# Revit family: 879-100X1X-001-DN50-600
name_source: partatom
category: Pipe Accessories
units: mm (PartAtom-declared; Revit-internal decimal feet)

## family parameters
Always vertical = Yes
Cut with Voids When Loaded = No
Part Type = Valve - Breaks Into
Round Connector Dimension = Use Diameter
Shared = No
Work Plane-Based = No

## types (38) — shared parameters
1 = 1 mm  [stored 0.00328084 ft]
879-0050-10-14400051199 = DN50_PN10/16
879-0050-10-144000511A0 = DN50_PN10/16
879-0065-10-14400051199 = DN65_PN10/16
879-0065-10-144000511A0 = DN65_PN10/16
879-0080-10-14400051199 = DN80_PN10/16
879-0080-10-144000511A0 = DN80_PN10/16
879-0100-10-14400051199 = DN100_PN10/16
879-0100-10-144000511A0 = DN100_PN10/16
879-0150-10-14400051199 = DN150_PN10/16
879-0150-10-144000511A0 = DN150_PN10/16
879-0200-10-04400051199 = DN200_PN10
879-0200-10-044000511A0 = DN200_PN10
879-0200-10-14400051199 = DN200_PN16
879-0200-10-144000511A0 = DN200_PN16
879-0300-10-04400051199 = DN300_PN10
879-0300-10-044000511A0 = DN300_PN10
879-0300-10-14400051199 = DN300_PN16
879-0300-10-144000511A0 = DN300_PN16
879-0350-10-04400051199 = DN350_PN10
879-0350-10-044000511A0 = DN350_PN10
879-0350-10-14400051199 = DN350_PN16
879-0350-10-144000511A0 = DN350_PN16
879-0400-10-04400051199 = DN400_PN10
879-0400-10-044000511A0 = DN400_PN10
879-0400-10-14400051199 = DN400_PN16
879-0400-10-144000511A0 = DN400_PN16
879-0450-10-04400051199 = DN450_PN10
879-0450-10-044000511A0 = DN450_PN10
879-0450-10-14400051199 = DN450_PN16
879-0450-10-144000511A0 = DN450_PN16
879-0500-10-04400051199 = DN500_PN10
879-0500-10-044000511A0 = DN500_PN10
879-0500-10-14400051199 = DN500_PN16
879-0500-10-144000511A0 = DN500_PN16
879-0600-10-04400051199 = DN600_PN10
879-0600-10-044000511A0 = DN600_PN10
879-0600-10-14400051199 = DN600_PN16
879-0600-10-144000511A0 = DN600_PN16
Body_wall_thickness = 10 mm  [stored 0.0328084 ft]
Description_ = AVK PRESS. RED./PRESS. SUST. CONTROL VALVE
Search_Table = 879-100X1X-001-DN50-600
URL product pages = https://www.avkvalves.com

## per-type parameters (varying)
- 879-0050-10-14400051199_DN50_PN10/16: Body_Collar_Dia=24 mm; Body_Collar_Dia_2=21 mm  [stored 0.0688976 ft]; Body_Flange_Dia=66 mm; Body_Flange_Dia_2=72 mm; Body_Height_1=58 mm; Body_Height_2=29 mm; Body_Height_3=45 mm; Body_Height_4=44 mm; Body_Top_Dia=10 mm  [stored 0.0328084 ft]; Body_Top_Dia_2=9 mm  [stored 0.0295276 ft]; Body_With_Dia=46 mm; Body_With_Dia_1=58 mm; Body_With_Dia_2=62 mm; Bolt_support=177 mm; Bolt_support_2=88 mm; Bolt_support_Dia=12 mm  [stored 0.0393701 ft]; Bolt_support_lenght=45 mm; Bolt_support_lenght_2=55 mm; Bottom_profile=13 mm; D1=50 mm; D3=83 mm; D3_Ref=221 mm; DN=50 mm; Fillet_Length=6 mm  [stored 0.019685 ft]; Flange_thickness=19 mm  [stored 0.062336 ft]; H3=405 mm; ID=25 mm  [stored 0.082021 ft]; L=230 mm; PG_Dia=25 mm  [stored 0.082021 ft]; PG_Ref=38 mm; PG_depth=8 mm  [stored 0.0262467 ft]; PG_height=207 mm; PG_height_1=195 mm; PG_ref=45 mm; PR_1=41 mm  [stored 0.134514 ft]; P_lenght=25 mm  [stored 0.082021 ft]; Pilot_Dia_1=15 mm  [stored 0.0492126 ft]; Pilot_Dia_2=23 mm  [stored 0.0754593 ft]; Pilot_Dia_3=10 mm  [stored 0.0328084 ft]; Pilot_Dia_4=5 mm  [stored 0.0164042 ft]; Pilot_Dia_5=3 mm  [stored 0.00984252 ft]; Pilot_top_1=234 mm; Pilot_top_ref=78 mm; Profile1_Height=100 mm; Profile1_Length=22 mm  [stored 0.0721785 ft]; Profile1_Length_2=15 mm  [stored 0.0492126 ft]; Profile_Dia=6 mm  [stored 0.019685 ft]; Profile_Dia_2=6 mm  [stored 0.019685 ft]; Profile_Dia_3=12 mm  [stored 0.0393701 ft]; Profile_height ref=41 mm  [stored 0.134514 ft]; T_Height=182 mm; T_Height_2=156 mm; T_Height_Ref_1=26 mm; T_Height_Ref_2=30 mm  [stored 0.0984252 ft]; Top_Profile=106 mm; Top_Profile_Ref=111 mm; W=295 mm; W_Ref=199 mm; W_ref_2=277 mm
- 879-0050-10-144000511A0_DN50_PN10/16: Body_Collar_Dia=24 mm; Body_Collar_Dia_2=21 mm  [stored 0.0688976 ft]; Body_Flange_Dia=66 mm; Body_Flange_Dia_2=72 mm; Body_Height_1=58 mm; Body_Height_2=29 mm; Body_Height_3=50 mm; Body_Height_4=44 mm; Body_Top_Dia=10 mm  [stored 0.0328084 ft]; Body_Top_Dia_2=9 mm  [stored 0.0295276 ft]; Body_With_Dia=46 mm; Body_With_Dia_1=58 mm; Body_With_Dia_2=62 mm; Bolt_support=177 mm; Bolt_support_2=88 mm; Bolt_support_Dia=12 mm  [stored 0.0393701 ft]; Bolt_support_lenght=45 mm; Bolt_support_lenght_2=55 mm; Bottom_profile=13 mm; D1=50 mm; D3=83 mm; D3_Ref=221 mm; DN=50 mm; Fillet_Length=6 mm  [stored 0.019685 ft]; Flange_thickness=19 mm  [stored 0.062336 ft]; H3=407 mm; ID=25 mm  [stored 0.082021 ft]; L=230 mm; PG_Dia=25 mm  [stored 0.082021 ft]; PG_Ref=38 mm; PG_depth=8 mm  [stored 0.0262467 ft]; PG_height=215 mm; PG_height_1=203 mm; PG_ref=45 mm; PR_1=39 mm; P_lenght=25 mm  [stored 0.082021 ft]; Pilot_Dia_1=15 mm  [stored 0.0492126 ft]; Pilot_Dia_2=23 mm  [stored 0.0754593 ft]; Pilot_Dia_3=10 mm  [stored 0.0328084 ft]; Pilot_Dia_4=5 mm  [stored 0.0164042 ft]; Pilot_Dia_5=3 mm  [stored 0.00984252 ft]; Pilot_top_1=238 mm; Pilot_top_ref=77 mm; Profile1_Height=110 mm; Profile1_Length=22 mm  [stored 0.0721785 ft]; Profile1_Length_2=15 mm  [stored 0.0492126 ft]; Profile_Dia=6 mm  [stored 0.019685 ft]; Profile_Dia_2=6 mm  [stored 0.019685 ft]; Profile_Dia_3=12 mm  [stored 0.0393701 ft]; Profile_height ref=41 mm  [stored 0.134514 ft]; T_Height=174 mm; T_Height_2=149 mm; T_Height_Ref_1=25 mm  [stored 0.082021 ft]; T_Height_Ref_2=29 mm; Top_Profile=106 mm; Top_Profile_Ref=111 mm; W=295 mm; W_Ref=199 mm; W_ref_2=277 mm
- 879-0065-10-14400051199_DN65_PN10/16: Body_Collar_Dia=30 mm  [stored 0.0984252 ft]; Body_Collar_Dia_2=26 mm; Body_Flange_Dia=83 mm; Body_Flange_Dia_2=91 mm; Body_Height_1=73 mm; Body_Height_2=36 mm  [stored 0.11811 ft]; Body_Height_3=58 mm; Body_Height_4=51 mm; Body_Top_Dia=13 mm; Body_Top_Dia_2=11 mm; Body_With_Dia=58 mm; Body_With_Dia_1=73 mm; Body_With_Dia_2=78 mm; Bolt_support=223 mm; Bolt_support_2=112 mm; Bolt_support_Dia=12 mm  [stored 0.0393701 ft]; Bolt_support_lenght=53 mm; Bolt_support_lenght_2=63 mm; Bottom_profile=16 mm  [stored 0.0524934 ft]; D1=59 mm; D3=93 mm; D3_Ref=246 mm; DN=65 mm; Fillet_Length=6 mm  [stored 0.019685 ft]; Flange_thickness=19 mm  [stored 0.062336 ft]; H3=435 mm; ID=33 mm  [stored 0.108268 ft]; L=290 mm; PG_Dia=33 mm  [stored 0.108268 ft]; PG_Ref=48 mm; PG_depth=8 mm  [stored 0.0262467 ft]; PG_height=232 mm; PG_height_1=216 mm; PG_ref=53 mm; PR_1=42 mm  [stored 0.137795 ft]; P_lenght=29 mm; Pilot_Dia_1=18 mm; Pilot_Dia_2=26 mm; Pilot_Dia_3=12 mm  [stored 0.0393701 ft]; Pilot_Dia_4=6 mm  [stored 0.019685 ft]; Pilot_Dia_5=4 mm  [stored 0.0131234 ft]; Pilot_top_1=262 mm; Pilot_top_ref=70 mm; Profile1_Height=117 mm; Profile1_Length=25 mm  [stored 0.082021 ft]; Profile1_Length_2=17 mm; Profile_Dia=6 mm  [stored 0.019685 ft]; Profile_Dia_2=6 mm  [stored 0.019685 ft]; Profile_Dia_3=12 mm  [stored 0.0393701 ft]; Profile_height ref=41 mm  [stored 0.134514 ft]; T_Height=185 mm; T_Height_2=158 mm; T_Height_Ref_1=26 mm; T_Height_Ref_2=31 mm  [stored 0.101706 ft]; Top_Profile=134 mm; Top_Profile_Ref=139 mm; W=325 mm; W_Ref=220 mm; W_ref_2=307 mm
- 879-0065-10-144000511A0_DN65_PN10/16: Body_Collar_Dia=30 mm  [stored 0.0984252 ft]; Body_Collar_Dia_2=26 mm; Body_Flange_Dia=83 mm; Body_Flange_Dia_2=91 mm; Body_Height_1=73 mm; Body_Height_2=36 mm  [stored 0.11811 ft]; Body_Height_3=73 mm; Body_Height_4=51 mm; Body_Top_Dia=13 mm; Body_Top_Dia_2=11 mm; Body_With_Dia=58 mm; Body_With_Dia_1=73 mm; Body_With_Dia_2=78 mm; Bolt_support=223 mm; Bolt_support_2=112 mm; Bolt_support_Dia=12 mm  [stored 0.0393701 ft]; Bolt_support_lenght=53 mm; Bolt_support_lenght_2=63 mm; Bottom_profile=16 mm  [stored 0.0524934 ft]; D1=59 mm; D3=93 mm; D3_Ref=246 mm; DN=65 mm; Fillet_Length=6 mm  [stored 0.019685 ft]; Flange_thickness=19 mm  [stored 0.062336 ft]; H3=436 mm; ID=33 mm  [stored 0.108268 ft]; L=290 mm; PG_Dia=33 mm  [stored 0.108268 ft]; PG_Ref=48 mm; PG_depth=8 mm  [stored 0.0262467 ft]; PG_height=246 mm; PG_height_1=230 mm; PG_ref=53 mm; PR_1=38 mm; P_lenght=29 mm; Pilot_Dia_1=18 mm; Pilot_Dia_2=26 mm; Pilot_Dia_3=12 mm  [stored 0.0393701 ft]; Pilot_Dia_4=6 mm  [stored 0.019685 ft]; Pilot_Dia_5=4 mm  [stored 0.0131234 ft]; Pilot_top_1=270 mm; Pilot_top_ref=64 mm; Profile1_Height=135 mm; Profile1_Length=25 mm  [stored 0.082021 ft]; Profile1_Length_2=17 mm; Profile_Dia=6 mm  [stored 0.019685 ft]; Profile_Dia_2=6 mm  [stored 0.019685 ft]; Profile_Dia_3=12 mm  [stored 0.0393701 ft]; Profile_height ref=41 mm  [stored 0.134514 ft]; T_Height=168 mm; T_Height_2=144 mm; T_Height_Ref_1=24 mm; T_Height_Ref_2=28 mm  [stored 0.0918635 ft]; Top_Profile=134 mm; Top_Profile_Ref=139 mm; W=325 mm; W_Ref=220 mm; W_ref_2=307 mm
- 879-0080-10-14400051199_DN80_PN10/16: Body_Collar_Dia=32 mm; Body_Collar_Dia_2=28 mm  [stored 0.0918635 ft]; Body_Flange_Dia=89 mm; Body_Flange_Dia_2=97 mm; Body_Height_1=78 mm; Body_Height_2=39 mm; Body_Height_3=62 mm; Body_Height_4=54 mm; Body_Top_Dia=14 mm  [stored 0.0459318 ft]; Body_Top_Dia_2=12 mm  [stored 0.0393701 ft]; Body_With_Dia=62 mm; Body_With_Dia_1=78 mm; Body_With_Dia_2=84 mm; Bolt_support=238 mm; Bolt_support_2=119 mm; Bolt_support_Dia=12 mm  [stored 0.0393701 ft]; Bolt_support_lenght=60 mm; Bolt_support_lenght_2=70 mm; Bottom_profile=20 mm  [stored 0.0656168 ft]; D1=66 mm; D3=100 mm; D3_Ref=264 mm; DN=80 mm; Fillet_Length=6 mm  [stored 0.019685 ft]; Flange_thickness=19 mm  [stored 0.062336 ft]; H3=450 mm; ID=40 mm  [stored 0.131234 ft]; L=310 mm; PG_Dia=40 mm  [stored 0.131234 ft]; PG_Ref=52 mm; PG_depth=8 mm  [stored 0.0262467 ft]; PG_height=262 mm; PG_height_1=242 mm; PG_ref=60 mm; PR_1=37 mm; P_lenght=32 mm; Pilot_Dia_1=20 mm  [stored 0.0656168 ft]; Pilot_Dia_2=29 mm; Pilot_Dia_3=13 mm; Pilot_Dia_4=7 mm  [stored 0.0229659 ft]; Pilot_Dia_5=4 mm  [stored 0.0131234 ft]; Pilot_top_1=272 mm; Pilot_top_ref=68 mm; Profile1_Height=144 mm; Profile1_Length=27 mm; Profile1_Length_2=18 mm; Profile_Dia=6 mm  [stored 0.019685 ft]; Profile_Dia_2=6 mm  [stored 0.019685 ft]; Profile_Dia_3=12 mm  [stored 0.0393701 ft]; Profile_height ref=41 mm  [stored 0.134514 ft]; T_Height=165 mm; T_Height_2=141 mm; T_Height_Ref_1=24 mm; T_Height_Ref_2=28 mm  [stored 0.0918635 ft]; Top_Profile=143 mm; Top_Profile_Ref=148 mm; W=345 mm; W_Ref=234 mm; W_ref_2=327 mm
- 879-0080-10-144000511A0_DN80_PN10/16: Body_Collar_Dia=32 mm; Body_Collar_Dia_2=28 mm  [stored 0.0918635 ft]; Body_Flange_Dia=89 mm; Body_Flange_Dia_2=97 mm; Body_Height_1=78 mm; Body_Height_2=39 mm; Body_Height_3=78 mm; Body_Height_4=54 mm; Body_Top_Dia=14 mm  [stored 0.0459318 ft]; Body_Top_Dia_2=12 mm  [stored 0.0393701 ft]; Body_With_Dia=62 mm; Body_With_Dia_1=78 mm; Body_With_Dia_2=84 mm; Bolt_support=238 mm; Bolt_support_2=119 mm; Bolt_support_Dia=12 mm  [stored 0.0393701 ft]; Bolt_support_lenght=60 mm; Bolt_support_lenght_2=70 mm; Bottom_profile=20 mm  [stored 0.0656168 ft]; D1=66 mm; D3=100 mm; D3_Ref=264 mm; DN=80 mm; Fillet_Length=6 mm  [stored 0.019685 ft]; Flange_thickness=19 mm  [stored 0.062336 ft]; H3=451 mm; ID=40 mm  [stored 0.131234 ft]; L=310 mm; PG_Dia=40 mm  [stored 0.131234 ft]; PG_Ref=52 mm; PG_depth=8 mm  [stored 0.0262467 ft]; PG_height=254 mm; PG_height_1=234 mm; PG_ref=60 mm; PR_1=40 mm  [stored 0.131234 ft]; P_lenght=32 mm; Pilot_Dia_1=20 mm  [stored 0.0656168 ft]; Pilot_Dia_2=29 mm; Pilot_Dia_3=13 mm; Pilot_Dia_4=7 mm  [stored 0.0229659 ft]; Pilot_Dia_5=4 mm  [stored 0.0131234 ft]; Pilot_top_1=280 mm; Pilot_top_ref=61 mm; Profile1_Height=133 mm; Profile1_Length=27 mm; Profile1_Length_2=18 mm; Profile_Dia=6 mm  [stored 0.019685 ft]; Profile_Dia_2=6 mm  [stored 0.019685 ft]; Profile_Dia_3=12 mm  [stored 0.0393701 ft]; Profile_height ref=41 mm  [stored 0.134514 ft]; T_Height=177 mm; T_Height_2=152 mm; T_Height_Ref_1=25 mm  [stored 0.082021 ft]; T_Height_Ref_2=30 mm  [stored 0.0984252 ft]; Top_Profile=143 mm; Top_Profile_Ref=148 mm; W=345 mm; W_Ref=234 mm; W_ref_2=327 mm
- 879-0100-10-14400051199_DN100_PN10/16: Body_Collar_Dia=36 mm  [stored 0.11811 ft]; Body_Collar_Dia_2=31 mm  [stored 0.101706 ft]; Body_Flange_Dia=100 mm; Body_Flange_Dia_2=109 mm; Body_Height_1=88 mm; Body_Height_2=44 mm; Body_Height_3=59 mm; Body_Height_4=59 mm; Body_Top_Dia=16 mm  [stored 0.0524934 ft]; Body_Top_Dia_2=13 mm; Body_With_Dia=70 mm; Body_With_Dia_1=88 mm; Body_With_Dia_2=95 mm; Bolt_support=269 mm; Bolt_support_2=135 mm; Bolt_support_Dia=12 mm  [stored 0.0393701 ft]; Bolt_support_lenght=70 mm; Bolt_support_lenght_2=80 mm; Bottom_profile=25 mm  [stored 0.082021 ft]; D1=78 mm; D3=110 mm; D3_Ref=296 mm; DN=100 mm; Fillet_Length=6 mm  [stored 0.019685 ft]; Flange_thickness=19 mm  [stored 0.062336 ft]; H3=470 mm; ID=50 mm; L=350 mm; PG_Dia=50 mm; PG_Ref=58 mm; PG_depth=8 mm  [stored 0.0262467 ft]; PG_height=279 mm; PG_height_1=254 mm; PG_ref=70 mm; PR_1=38 mm; P_lenght=36 mm  [stored 0.11811 ft]; Pilot_Dia_1=22 mm  [stored 0.0721785 ft]; Pilot_Dia_2=33 mm  [stored 0.108268 ft]; Pilot_Dia_3=15 mm  [stored 0.0492126 ft]; Pilot_Dia_4=7 mm  [stored 0.0229659 ft]; Pilot_Dia_5=5 mm  [stored 0.0164042 ft]; Pilot_top_1=282 mm; Pilot_top_ref=68 mm; Profile1_Height=150 mm; Profile1_Length=30 mm  [stored 0.0984252 ft]; Profile1_Length_2=20 mm  [stored 0.0656168 ft]; Profile_Dia=6 mm  [stored 0.019685 ft]; Profile_Dia_2=6 mm  [stored 0.019685 ft]; Profile_Dia_3=12 mm  [stored 0.0393701 ft]; Profile_height ref=41 mm  [stored 0.134514 ft]; T_Height=169 mm; T_Height_2=145 mm; T_Height_Ref_1=24 mm; T_Height_Ref_2=28 mm  [stored 0.0918635 ft]; Top_Profile=162 mm; Top_Profile_Ref=167 mm; W=390 mm; W_Ref=263 mm; W_ref_2=372 mm
- 879-0100-10-144000511A0_DN100_PN10/16: Body_Collar_Dia=36 mm  [stored 0.11811 ft]; Body_Collar_Dia_2=31 mm  [stored 0.101706 ft]; Body_Flange_Dia=100 mm; Body_Flange_Dia_2=109 mm; Body_Height_1=88 mm; Body_Height_2=44 mm; Body_Height_3=70 mm; Body_Height_4=59 mm; Body_Top_Dia=16 mm  [stored 0.0524934 ft]; Body_Top_Dia_2=13 mm; Body_With_Dia=70 mm; Body_With_Dia_1=88 mm; Body_With_Dia_2=95 mm; Bolt_support=269 mm; Bolt_support_2=135 mm; Bolt_support_Dia=12 mm  [stored 0.0393701 ft]; Bolt_support_lenght=70 mm; Bolt_support_lenght_2=80 mm; Bottom_profile=25 mm  [stored 0.082021 ft]; D1=78 mm; D3=110 mm; D3_Ref=296 mm; DN=100 mm; Fillet_Length=6 mm  [stored 0.019685 ft]; Flange_thickness=19 mm  [stored 0.062336 ft]; H3=474 mm; ID=50 mm; L=350 mm; PG_Dia=50 mm; PG_Ref=58 mm; PG_depth=8 mm  [stored 0.0262467 ft]; PG_height=273 mm; PG_height_1=248 mm; PG_ref=70 mm; PR_1=41 mm  [stored 0.134514 ft]; P_lenght=36 mm  [stored 0.11811 ft]; Pilot_Dia_1=22 mm  [stored 0.0721785 ft]; Pilot_Dia_2=33 mm  [stored 0.108268 ft]; Pilot_Dia_3=15 mm  [stored 0.0492126 ft]; Pilot_Dia_4=7 mm  [stored 0.0229659 ft]; Pilot_Dia_5=5 mm  [stored 0.0164042 ft]; Pilot_top_1=290 mm; Pilot_top_ref=64 mm; Profile1_Height=141 mm; Profile1_Length=30 mm  [stored 0.0984252 ft]; Profile1_Length_2=20 mm  [stored 0.0656168 ft]; Profile_Dia=6 mm  [stored 0.019685 ft]; Profile_Dia_2=6 mm  [stored 0.019685 ft]; Profile_Dia_3=12 mm  [stored 0.0393701 ft]; Profile_height ref=41 mm  [stored 0.134514 ft]; T_Height=182 mm; T_Height_2=156 mm; T_Height_Ref_1=26 mm; T_Height_Ref_2=30 mm  [stored 0.0984252 ft]; Top_Profile=162 mm; Top_Profile_Ref=167 mm; W=390 mm; W_Ref=263 mm; W_ref_2=372 mm
- 879-0150-10-14400051199_DN150_PN10/16: Body_Collar_Dia=50 mm; Body_Collar_Dia_2=43 mm; Body_Flange_Dia=137 mm; Body_Flange_Dia_2=150 mm; Body_Height_1=120 mm; Body_Height_2=60 mm; Body_Height_3=60 mm; Body_Height_4=75 mm; Body_Top_Dia=22 mm  [stored 0.0721785 ft]; Body_Top_Dia_2=18 mm; Body_With_Dia=96 mm; Body_With_Dia_1=120 mm; Body_With_Dia_2=130 mm; Bolt_support=369 mm; Bolt_support_2=185 mm; Bolt_support_Dia=16 mm  [stored 0.0524934 ft]; Bolt_support_lenght=95 mm; Bolt_support_lenght_2=105 mm; Bottom_profile=38 mm; D1=106 mm; D3=143 mm; D3_Ref=373 mm; DN=150 mm; Fillet_Length=8 mm  [stored 0.0262467 ft]; Flange_thickness=19 mm  [stored 0.062336 ft]; H3=605 mm; ID=75 mm; L=480 mm; PG_Dia=50 mm; PG_Ref=80 mm; PG_depth=11 mm; PG_height=339 mm; PG_height_1=314 mm; PG_ref=95 mm; PR_1=51 mm; P_lenght=51 mm; Pilot_Dia_1=31 mm  [stored 0.101706 ft]; Pilot_Dia_2=47 mm; Pilot_Dia_3=21 mm  [stored 0.0688976 ft]; Pilot_Dia_4=10 mm  [stored 0.0328084 ft]; Pilot_Dia_5=7 mm  [stored 0.0229659 ft]; Pilot_top_1=359 mm; Pilot_top_ref=94 mm; Profile1_Height=195 mm; Profile1_Length=39 mm; Profile1_Length_2=26 mm; Profile_Dia=8 mm  [stored 0.0262467 ft]; Profile_Dia_2=8 mm  [stored 0.0262467 ft]; Profile_Dia_3=16 mm  [stored 0.0524934 ft]; Profile_height ref=43 mm; T_Height=225 mm; T_Height_2=192 mm; T_Height_Ref_1=32 mm; T_Height_Ref_2=37 mm; Top_Profile=222 mm; Top_Profile_Ref=227 mm; W=485 mm; W_Ref=327 mm; W_ref_2=461 mm
- 879-0150-10-144000511A0_DN150_PN10/16: Body_Collar_Dia=50 mm; Body_Collar_Dia_2=43 mm; Body_Flange_Dia=137 mm; Body_Flange_Dia_2=150 mm; Body_Height_1=120 mm; Body_Height_2=60 mm; Body_Height_3=68 mm; Body_Height_4=75 mm; Body_Top_Dia=22 mm  [stored 0.0721785 ft]; Body_Top_Dia_2=18 mm; Body_With_Dia=96 mm; Body_With_Dia_1=120 mm; Body_With_Dia_2=130 mm; Bolt_support=369 mm; Bolt_support_2=185 mm; Bolt_support_Dia=16 mm  [stored 0.0524934 ft]; Bolt_support_lenght=95 mm; Bolt_support_lenght_2=105 mm; Bottom_profile=38 mm; D1=106 mm; D3=143 mm; D3_Ref=373 mm; DN=150 mm; Fillet_Length=8 mm  [stored 0.0262467 ft]; Flange_thickness=19 mm  [stored 0.062336 ft]; H3=607 mm; ID=75 mm; L=480 mm; PG_Dia=50 mm; PG_Ref=80 mm; PG_depth=11 mm; PG_height=339 mm; PG_height_1=314 mm; PG_ref=95 mm; PR_1=51 mm; P_lenght=51 mm; Pilot_Dia_1=31 mm  [stored 0.101706 ft]; Pilot_Dia_2=47 mm; Pilot_Dia_3=21 mm  [stored 0.0688976 ft]; Pilot_Dia_4=10 mm  [stored 0.0328084 ft]; Pilot_Dia_5=7 mm  [stored 0.0229659 ft]; Pilot_top_1=364 mm; Pilot_top_ref=91 mm; Profile1_Height=195 mm; Profile1_Length=39 mm; Profile1_Length_2=26 mm; Profile_Dia=8 mm  [stored 0.0262467 ft]; Profile_Dia_2=8 mm  [stored 0.0262467 ft]; Profile_Dia_3=16 mm  [stored 0.0524934 ft]; Profile_height ref=43 mm; T_Height=227 mm; T_Height_2=194 mm; T_Height_Ref_1=32 mm; T_Height_Ref_2=38 mm; Top_Profile=222 mm; Top_Profile_Ref=227 mm; W=485 mm; W_Ref=327 mm; W_ref_2=461 mm
- 879-0200-10-04400051199_DN200_PN10: Body_Collar_Dia=63 mm; Body_Collar_Dia_2=54 mm; Body_Flange_Dia=171 mm; Body_Flange_Dia_2=188 mm; Body_Height_1=150 mm; Body_Height_2=75 mm; Body_Height_3=75 mm; Body_Height_4=90 mm; Body_Top_Dia=27 mm; Body_Top_Dia_2=22 mm  [stored 0.0721785 ft]; Body_With_Dia=120 mm; Body_With_Dia_1=150 mm; Body_With_Dia_2=162 mm; Bolt_support=462 mm; Bolt_support_2=231 mm; Bolt_support_Dia=20 mm  [stored 0.0656168 ft]; Bolt_support_lenght=120 mm; Bolt_support_lenght_2=130 mm; Bottom_profile=50 mm; D1=133 mm; D3=170 mm; D3_Ref=428 mm; DN=200 mm; Fillet_Length=10 mm  [stored 0.0328084 ft]; Flange_thickness=20 mm  [stored 0.0656168 ft]; H3=720 mm; ID=100 mm; L=600 mm; PG_Dia=67 mm; PG_Ref=100 mm; PG_depth=14 mm  [stored 0.0459318 ft]; PG_height=410 mm; PG_height_1=377 mm; PG_ref=120 mm; PR_1=60 mm; P_lenght=64 mm; Pilot_Dia_1=39 mm; Pilot_Dia_2=58 mm; Pilot_Dia_3=26 mm; Pilot_Dia_4=13 mm; Pilot_Dia_5=9 mm  [stored 0.0295276 ft]; Pilot_top_1=433 mm; Pilot_top_ref=108 mm; Profile1_Height=238 mm; Profile1_Length=46 mm; Profile1_Length_2=31 mm  [stored 0.101706 ft]; Profile_Dia=10 mm  [stored 0.0328084 ft]; Profile_Dia_2=10 mm  [stored 0.0328084 ft]; Profile_Dia_3=20 mm  [stored 0.0656168 ft]; Profile_height ref=45 mm; T_Height=267 mm; T_Height_2=229 mm; T_Height_Ref_1=38 mm; T_Height_Ref_2=45 mm; Top_Profile=277 mm; Top_Profile_Ref=282 mm; W=545 mm; W_Ref=370 mm; W_ref_2=515 mm
- 879-0200-10-044000511A0_DN200_PN10: Body_Collar_Dia=63 mm; Body_Collar_Dia_2=54 mm; Body_Flange_Dia=171 mm; Body_Flange_Dia_2=188 mm; Body_Height_1=150 mm; Body_Height_2=75 mm; Body_Height_3=100 mm; Body_Height_4=90 mm; Body_Top_Dia=27 mm; Body_Top_Dia_2=22 mm  [stored 0.0721785 ft]; Body_With_Dia=120 mm; Body_With_Dia_1=150 mm; Body_With_Dia_2=162 mm; Bolt_support=462 mm; Bolt_support_2=231 mm; Bolt_support_Dia=20 mm  [stored 0.0656168 ft]; Bolt_support_lenght=120 mm; Bolt_support_lenght_2=130 mm; Bottom_profile=50 mm; D1=133 mm; D3=170 mm; D3_Ref=428 mm; DN=200 mm; Fillet_Length=10 mm  [stored 0.0328084 ft]; Flange_thickness=20 mm  [stored 0.0656168 ft]; H3=774 mm; ID=100 mm; L=600 mm; PG_Dia=67 mm; PG_Ref=100 mm; PG_depth=14 mm  [stored 0.0459318 ft]; PG_height=424 mm; PG_height_1=391 mm; PG_ref=120 mm; PR_1=72 mm; P_lenght=64 mm; Pilot_Dia_1=39 mm; Pilot_Dia_2=58 mm; Pilot_Dia_3=26 mm; Pilot_Dia_4=13 mm; Pilot_Dia_5=9 mm  [stored 0.0295276 ft]; Pilot_top_1=472 mm; Pilot_top_ref=122 mm; Profile1_Height=240 mm; Profile1_Length=46 mm; Profile1_Length_2=31 mm  [stored 0.101706 ft]; Profile_Dia=10 mm  [stored 0.0328084 ft]; Profile_Dia_2=10 mm  [stored 0.0328084 ft]; Profile_Dia_3=20 mm  [stored 0.0656168 ft]; Profile_height ref=45 mm; T_Height=319 mm; T_Height_2=273 mm; T_Height_Ref_1=46 mm; T_Height_Ref_2=53 mm; Top_Profile=277 mm; Top_Profile_Ref=282 mm; W=545 mm; W_Ref=370 mm; W_ref_2=515 mm
- 879-0200-10-14400051199_DN200_PN16: Body_Collar_Dia=63 mm; Body_Collar_Dia_2=54 mm; Body_Flange_Dia=171 mm; Body_Flange_Dia_2=188 mm; Body_Height_1=150 mm; Body_Height_2=75 mm; Body_Height_3=75 mm; Body_Height_4=90 mm; Body_Top_Dia=27 mm; Body_Top_Dia_2=22 mm  [stored 0.0721785 ft]; Body_With_Dia=120 mm; Body_With_Dia_1=150 mm; Body_With_Dia_2=162 mm; Bolt_support=462 mm; Bolt_support_2=231 mm; Bolt_support_Dia=20 mm  [stored 0.0656168 ft]; Bolt_support_lenght=120 mm; Bolt_support_lenght_2=130 mm; Bottom_profile=50 mm; D1=133 mm; D3=170 mm; D3_Ref=428 mm; DN=200 mm; Fillet_Length=10 mm  [stored 0.0328084 ft]; Flange_thickness=20 mm  [stored 0.0656168 ft]; H3=720 mm; ID=100 mm; L=600 mm; PG_Dia=67 mm; PG_Ref=100 mm; PG_depth=14 mm  [stored 0.0459318 ft]; PG_height=410 mm; PG_height_1=377 mm; PG_ref=120 mm; PR_1=60 mm; P_lenght=64 mm; Pilot_Dia_1=39 mm; Pilot_Dia_2=58 mm; Pilot_Dia_3=26 mm; Pilot_Dia_4=13 mm; Pilot_Dia_5=9 mm  [stored 0.0295276 ft]; Pilot_top_1=433 mm; Pilot_top_ref=108 mm; Profile1_Height=238 mm; Profile1_Length=46 mm; Profile1_Length_2=31 mm  [stored 0.101706 ft]; Profile_Dia=10 mm  [stored 0.0328084 ft]; Profile_Dia_2=10 mm  [stored 0.0328084 ft]; Profile_Dia_3=20 mm  [stored 0.0656168 ft]; Profile_height ref=45 mm; T_Height=267 mm; T_Height_2=229 mm; T_Height_Ref_1=38 mm; T_Height_Ref_2=45 mm; Top_Profile=277 mm; Top_Profile_Ref=282 mm; W=545 mm; W_Ref=370 mm; W_ref_2=515 mm
- 879-0200-10-144000511A0_DN200_PN16: Body_Collar_Dia=63 mm; Body_Collar_Dia_2=54 mm; Body_Flange_Dia=171 mm; Body_Flange_Dia_2=188 mm; Body_Height_1=150 mm; Body_Height_2=75 mm; Body_Height_3=86 mm; Body_Height_4=90 mm; Body_Top_Dia=27 mm; Body_Top_Dia_2=22 mm  [stored 0.0721785 ft]; Body_With_Dia=120 mm; Body_With_Dia_1=150 mm; Body_With_Dia_2=162 mm; Bolt_support=462 mm; Bolt_support_2=231 mm; Bolt_support_Dia=20 mm  [stored 0.0656168 ft]; Bolt_support_lenght=120 mm; Bolt_support_lenght_2=130 mm; Bottom_profile=50 mm; D1=133 mm; D3=170 mm; D3_Ref=428 mm; DN=200 mm; Fillet_Length=10 mm  [stored 0.0328084 ft]; Flange_thickness=20 mm  [stored 0.0656168 ft]; H3=774 mm; ID=100 mm; L=600 mm; PG_Dia=67 mm; PG_Ref=100 mm; PG_depth=14 mm  [stored 0.0459318 ft]; PG_height=424 mm; PG_height_1=391 mm; PG_ref=120 mm; PR_1=72 mm; P_lenght=64 mm; Pilot_Dia_1=39 mm; Pilot_Dia_2=58 mm; Pilot_Dia_3=26 mm; Pilot_Dia_4=13 mm; Pilot_Dia_5=9 mm  [stored 0.0295276 ft]; Pilot_top_1=465 mm; Pilot_top_ref=129 mm; Profile1_Height=240 mm; Profile1_Length=46 mm; Profile1_Length_2=31 mm  [stored 0.101706 ft]; Profile_Dia=10 mm  [stored 0.0328084 ft]; Profile_Dia_2=10 mm  [stored 0.0328084 ft]; Profile_Dia_3=20 mm  [stored 0.0656168 ft]; Profile_height ref=45 mm; T_Height=319 mm; T_Height_2=273 mm; T_Height_Ref_1=46 mm; T_Height_Ref_2=53 mm; Top_Profile=277 mm; Top_Profile_Ref=282 mm; W=545 mm; W_Ref=370 mm; W_ref_2=515 mm
- 879-0300-10-04400051199_DN300_PN10: Body_Collar_Dia=89 mm; Body_Collar_Dia_2=76 mm; Body_Flange_Dia=243 mm; Body_Flange_Dia_2=266 mm; Body_Height_1=213 mm; Body_Height_2=106 mm; Body_Height_3=95 mm; Body_Height_4=121 mm; Body_Top_Dia=38 mm; Body_Top_Dia_2=32 mm; Body_With_Dia=170 mm; Body_With_Dia_1=213 mm; Body_With_Dia_2=230 mm; Bolt_support=654 mm; Bolt_support_2=327 mm; Bolt_support_Dia=20 mm  [stored 0.0656168 ft]; Bolt_support_lenght=170 mm; Bolt_support_lenght_2=180 mm; Bottom_profile=75 mm; D1=185 mm; D3=223 mm; D3_Ref=515 mm; DN=300 mm; Fillet_Length=10 mm  [stored 0.0328084 ft]; Flange_thickness=25 mm  [stored 0.082021 ft]; H3=830 mm; ID=150 mm; L=850 mm; PG_Dia=100 mm; PG_Ref=142 mm; PG_depth=14 mm  [stored 0.0459318 ft]; PG_height=508 mm; PG_height_1=458 mm; PG_ref=170 mm; PR_1=58 mm; P_lenght=87 mm; Pilot_Dia_1=53 mm; Pilot_Dia_2=79 mm; Pilot_Dia_3=35 mm  [stored 0.114829 ft]; Pilot_Dia_4=18 mm; Pilot_Dia_5=12 mm  [stored 0.0393701 ft]; Pilot_top_1=518 mm; Pilot_top_ref=80 mm; Profile1_Height=305 mm; Profile1_Length=60 mm; Profile1_Length_2=40 mm  [stored 0.131234 ft]; Profile_Dia=10 mm  [stored 0.0328084 ft]; Profile_Dia_2=10 mm  [stored 0.0328084 ft]; Profile_Dia_3=20 mm  [stored 0.0656168 ft]; Profile_height ref=45 mm; T_Height=258 mm; T_Height_2=221 mm; T_Height_Ref_1=37 mm; T_Height_Ref_2=43 mm; Top_Profile=392 mm; Top_Profile_Ref=397 mm; W=615 mm; W_Ref=436 mm; W_ref_2=585 mm
- 879-0300-10-044000511A0_DN300_PN10: Body_Collar_Dia=89 mm; Body_Collar_Dia_2=76 mm; Body_Flange_Dia=243 mm; Body_Flange_Dia_2=266 mm; Body_Height_1=213 mm; Body_Height_2=106 mm; Body_Height_3=106 mm; Body_Height_4=121 mm; Body_Top_Dia=38 mm; Body_Top_Dia_2=32 mm; Body_With_Dia=170 mm; Body_With_Dia_1=213 mm; Body_With_Dia_2=230 mm; Bolt_support=654 mm; Bolt_support_2=327 mm; Bolt_support_Dia=20 mm  [stored 0.0656168 ft]; Bolt_support_lenght=170 mm; Bolt_support_lenght_2=180 mm; Bottom_profile=75 mm; D1=185 mm; D3=223 mm; D3_Ref=515 mm; DN=300 mm; Fillet_Length=10 mm  [stored 0.0328084 ft]; Flange_thickness=25 mm  [stored 0.082021 ft]; H3=923 mm; ID=150 mm; L=850 mm; PG_Dia=100 mm; PG_Ref=142 mm; PG_depth=14 mm  [stored 0.0459318 ft]; PG_height=553 mm; PG_height_1=503 mm; PG_ref=170 mm; PR_1=72 mm; P_lenght=87 mm; Pilot_Dia_1=53 mm; Pilot_Dia_2=79 mm; Pilot_Dia_3=35 mm  [stored 0.114829 ft]; Pilot_Dia_4=18 mm; Pilot_Dia_5=12 mm  [stored 0.0393701 ft]; Pilot_top_1=570 mm; Pilot_top_ref=120 mm; Profile1_Height=335 mm; Profile1_Length=60 mm; Profile1_Length_2=40 mm  [stored 0.131234 ft]; Profile_Dia=10 mm  [stored 0.0328084 ft]; Profile_Dia_2=10 mm  [stored 0.0328084 ft]; Profile_Dia_3=20 mm  [stored 0.0656168 ft]; Profile_height ref=45 mm; T_Height=321 mm; T_Height_2=275 mm; T_Height_Ref_1=46 mm; T_Height_Ref_2=53 mm; Top_Profile=392 mm; Top_Profile_Ref=397 mm; W=615 mm; W_Ref=436 mm; W_ref_2=585 mm
- 879-0300-10-14400051199_DN300_PN16: Body_Collar_Dia=89 mm; Body_Collar_Dia_2=76 mm; Body_Flange_Dia=243 mm; Body_Flange_Dia_2=266 mm; Body_Height_1=213 mm; Body_Height_2=106 mm; Body_Height_3=95 mm; Body_Height_4=121 mm; Body_Top_Dia=38 mm; Body_Top_Dia_2=32 mm; Body_With_Dia=170 mm; Body_With_Dia_1=213 mm; Body_With_Dia_2=230 mm; Bolt_support=654 mm; Bolt_support_2=327 mm; Bolt_support_Dia=20 mm  [stored 0.0656168 ft]; Bolt_support_lenght=170 mm; Bolt_support_lenght_2=180 mm; Bottom_profile=75 mm; D1=185 mm; D3=230 mm; D3_Ref=523 mm; DN=300 mm; Fillet_Length=10 mm  [stored 0.0328084 ft]; Flange_thickness=25 mm  [stored 0.082021 ft]; H3=830 mm; ID=150 mm; L=850 mm; PG_Dia=100 mm; PG_Ref=142 mm; PG_depth=14 mm  [stored 0.0459318 ft]; PG_height=507 mm; PG_height_1=457 mm; PG_ref=170 mm; PR_1=57 mm; P_lenght=90 mm; Pilot_Dia_1=55 mm; Pilot_Dia_2=82 mm; Pilot_Dia_3=36 mm  [stored 0.11811 ft]; Pilot_Dia_4=18 mm; Pilot_Dia_5=12 mm  [stored 0.0393701 ft]; Pilot_top_1=514 mm; Pilot_top_ref=76 mm; Profile1_Height=305 mm; Profile1_Length=62 mm; Profile1_Length_2=41 mm  [stored 0.134514 ft]; Profile_Dia=10 mm  [stored 0.0328084 ft]; Profile_Dia_2=10 mm  [stored 0.0328084 ft]; Profile_Dia_3=20 mm  [stored 0.0656168 ft]; Profile_height ref=45 mm; T_Height=250 mm; T_Height_2=214 mm; T_Height_Ref_1=36 mm  [stored 0.11811 ft]; T_Height_Ref_2=42 mm  [stored 0.137795 ft]; Top_Profile=392 mm; Top_Profile_Ref=397 mm; W=615 mm; W_Ref=441 mm; W_ref_2=585 mm
- 879-0300-10-144000511A0_DN300_PN16: Body_Collar_Dia=89 mm; Body_Collar_Dia_2=76 mm; Body_Flange_Dia=243 mm; Body_Flange_Dia_2=266 mm; Body_Height_1=213 mm; Body_Height_2=106 mm; Body_Height_3=95 mm; Body_Height_4=121 mm; Body_Top_Dia=38 mm; Body_Top_Dia_2=32 mm; Body_With_Dia=170 mm; Body_With_Dia_1=213 mm; Body_With_Dia_2=230 mm; Bolt_support=654 mm; Bolt_support_2=327 mm; Bolt_support_Dia=20 mm  [stored 0.0656168 ft]; Bolt_support_lenght=170 mm; Bolt_support_lenght_2=180 mm; Bottom_profile=75 mm; D1=185 mm; D3=230 mm; D3_Ref=523 mm; DN=300 mm; Fillet_Length=10 mm  [stored 0.0328084 ft]; Flange_thickness=25 mm  [stored 0.082021 ft]; H3=923 mm; ID=150 mm; L=850 mm; PG_Dia=100 mm; PG_Ref=142 mm; PG_depth=14 mm  [stored 0.0459318 ft]; PG_height=543 mm; PG_height_1=493 mm; PG_ref=170 mm; PR_1=73 mm; P_lenght=90 mm; Pilot_Dia_1=55 mm; Pilot_Dia_2=82 mm; Pilot_Dia_3=36 mm  [stored 0.11811 ft]; Pilot_Dia_4=18 mm; Pilot_Dia_5=12 mm  [stored 0.0393701 ft]; Pilot_top_1=561 mm; Pilot_top_ref=122 mm; Profile1_Height=325 mm; Profile1_Length=62 mm; Profile1_Length_2=41 mm  [stored 0.134514 ft]; Profile_Dia=10 mm  [stored 0.0328084 ft]; Profile_Dia_2=10 mm  [stored 0.0328084 ft]; Profile_Dia_3=20 mm  [stored 0.0656168 ft]; Profile_height ref=45 mm; T_Height=323 mm; T_Height_2=277 mm; T_Height_Ref_1=46 mm; T_Height_Ref_2=54 mm; Top_Profile=392 mm; Top_Profile_Ref=397 mm; W=615 mm; W_Ref=441 mm; W_ref_2=585 mm
- 879-0350-10-04400051199_DN350_PN10: Body_Collar_Dia=102 mm; Body_Collar_Dia_2=88 mm; Body_Flange_Dia=280 mm; Body_Flange_Dia_2=306 mm; Body_Height_1=245 mm; Body_Height_2=123 mm; Body_Height_3=98 mm; Body_Height_4=138 mm; Body_Top_Dia=44 mm; Body_Top_Dia_2=37 mm; Body_With_Dia=196 mm; Body_With_Dia_1=245 mm; Body_With_Dia_2=265 mm; Bolt_support=754 mm; Bolt_support_2=377 mm; Bolt_support_Dia=30 mm  [stored 0.0984252 ft]; Bolt_support_lenght=195 mm; Bolt_support_lenght_2=205 mm; Bottom_profile=88 mm; D1=215 mm; D3=253 mm; D3_Ref=590 mm; DN=350 mm; Fillet_Length=15 mm  [stored 0.0492126 ft]; Flange_thickness=27 mm; H3=950 mm; ID=175 mm; L=980 mm; PG_Dia=117 mm; PG_Ref=163 mm; PG_depth=21 mm  [stored 0.0688976 ft]; PG_height=580 mm; PG_height_1=522 mm; PG_ref=195 mm; PR_1=68 mm; P_lenght=100 mm; Pilot_Dia_1=61 mm; Pilot_Dia_2=91 mm; Pilot_Dia_3=40 mm  [stored 0.131234 ft]; Pilot_Dia_4=20 mm  [stored 0.0656168 ft]; Pilot_Dia_5=13 mm; Pilot_top_1=589 mm; Pilot_top_ref=99 mm; Profile1_Height=345 mm; Profile1_Length=68 mm; Profile1_Length_2=45 mm; Profile_Dia=15 mm  [stored 0.0492126 ft]; Profile_Dia_2=15 mm  [stored 0.0492126 ft]; Profile_Dia_3=30 mm  [stored 0.0984252 ft]; Profile_height ref=50 mm; T_Height=303 mm; T_Height_2=259 mm; T_Height_Ref_1=43 mm; T_Height_Ref_2=50 mm; Top_Profile=452 mm; Top_Profile_Ref=457 mm; W=720 mm; W_Ref=499 mm; W_ref_2=675 mm
- 879-0350-10-044000511A0_DN350_PN10: Body_Collar_Dia=102 mm; Body_Collar_Dia_2=88 mm; Body_Flange_Dia=280 mm; Body_Flange_Dia_2=306 mm; Body_Height_1=245 mm; Body_Height_2=123 mm; Body_Height_3=98 mm; Body_Height_4=138 mm; Body_Top_Dia=44 mm; Body_Top_Dia_2=37 mm; Body_With_Dia=196 mm; Body_With_Dia_1=245 mm; Body_With_Dia_2=265 mm; Bolt_support=754 mm; Bolt_support_2=377 mm; Bolt_support_Dia=30 mm  [stored 0.0984252 ft]; Bolt_support_lenght=195 mm; Bolt_support_lenght_2=205 mm; Bottom_profile=88 mm; D1=215 mm; D3=253 mm; D3_Ref=590 mm; DN=350 mm; Fillet_Length=15 mm  [stored 0.0492126 ft]; Flange_thickness=27 mm; H3=1045 mm; ID=175 mm; L=980 mm; PG_Dia=117 mm; PG_Ref=163 mm; PG_depth=21 mm  [stored 0.0688976 ft]; PG_height=602 mm; PG_height_1=543 mm; PG_ref=195 mm; PR_1=90 mm; P_lenght=100 mm; Pilot_Dia_1=61 mm; Pilot_Dia_2=91 mm; Pilot_Dia_3=40 mm  [stored 0.131234 ft]; Pilot_Dia_4=20 mm  [stored 0.0656168 ft]; Pilot_Dia_5=13 mm; Pilot_top_1=637 mm; Pilot_top_ref=146 mm; Profile1_Height=345 mm; Profile1_Length=68 mm; Profile1_Length_2=45 mm; Profile_Dia=15 mm  [stored 0.0492126 ft]; Profile_Dia_2=15 mm  [stored 0.0492126 ft]; Profile_Dia_3=30 mm  [stored 0.0984252 ft]; Profile_height ref=50 mm; T_Height=398 mm; T_Height_2=341 mm; T_Height_Ref_1=57 mm; T_Height_Ref_2=66 mm; Top_Profile=452 mm; Top_Profile_Ref=457 mm; W=720 mm; W_Ref=499 mm; W_ref_2=675 mm
- 879-0350-10-14400051199_DN350_PN16: Body_Collar_Dia=102 mm; Body_Collar_Dia_2=88 mm; Body_Flange_Dia=280 mm; Body_Flange_Dia_2=306 mm; Body_Height_1=245 mm; Body_Height_2=123 mm; Body_Height_3=89 mm; Body_Height_4=138 mm; Body_Top_Dia=44 mm; Body_Top_Dia_2=37 mm; Body_With_Dia=196 mm; Body_With_Dia_1=245 mm; Body_With_Dia_2=265 mm; Bolt_support=754 mm; Bolt_support_2=377 mm; Bolt_support_Dia=30 mm  [stored 0.0984252 ft]; Bolt_support_lenght=195 mm; Bolt_support_lenght_2=205 mm; Bottom_profile=88 mm; D1=215 mm; D3=260 mm; D3_Ref=598 mm; DN=350 mm; Fillet_Length=15 mm  [stored 0.0492126 ft]; Flange_thickness=27 mm; H3=950 mm; ID=175 mm; L=980 mm; PG_Dia=117 mm; PG_Ref=163 mm; PG_depth=21 mm  [stored 0.0688976 ft]; PG_height=578 mm; PG_height_1=520 mm; PG_ref=195 mm; PR_1=67 mm; P_lenght=104 mm; Pilot_Dia_1=63 mm; Pilot_Dia_2=95 mm; Pilot_Dia_3=42 mm  [stored 0.137795 ft]; Pilot_Dia_4=21 mm  [stored 0.0688976 ft]; Pilot_Dia_5=14 mm  [stored 0.0459318 ft]; Pilot_top_1=581 mm; Pilot_top_ref=99 mm; Profile1_Height=345 mm; Profile1_Length=70 mm; Profile1_Length_2=47 mm; Profile_Dia=15 mm  [stored 0.0492126 ft]; Profile_Dia_2=15 mm  [stored 0.0492126 ft]; Profile_Dia_3=30 mm  [stored 0.0984252 ft]; Profile_height ref=50 mm; T_Height=295 mm; T_Height_2=253 mm; T_Height_Ref_1=42 mm  [stored 0.137795 ft]; T_Height_Ref_2=49 mm; Top_Profile=452 mm; Top_Profile_Ref=457 mm; W=720 mm; W_Ref=503 mm; W_ref_2=675 mm
- 879-0350-10-144000511A0_DN350_PN16: Body_Collar_Dia=102 mm; Body_Collar_Dia_2=88 mm; Body_Flange_Dia=280 mm; Body_Flange_Dia_2=306 mm; Body_Height_1=245 mm; Body_Height_2=123 mm; Body_Height_3=89 mm; Body_Height_4=138 mm; Body_Top_Dia=44 mm; Body_Top_Dia_2=37 mm; Body_With_Dia=196 mm; Body_With_Dia_1=245 mm; Body_With_Dia_2=265 mm; Bolt_support=754 mm; Bolt_support_2=377 mm; Bolt_support_Dia=30 mm  [stored 0.0984252 ft]; Bolt_support_lenght=195 mm; Bolt_support_lenght_2=205 mm; Bottom_profile=88 mm; D1=215 mm; D3=260 mm; D3_Ref=598 mm; DN=350 mm; Fillet_Length=15 mm  [stored 0.0492126 ft]; Flange_thickness=27 mm; H3=1045 mm; ID=175 mm; L=980 mm; PG_Dia=117 mm; PG_Ref=163 mm; PG_depth=21 mm  [stored 0.0688976 ft]; PG_height=608 mm; PG_height_1=549 mm; PG_ref=195 mm; PR_1=86 mm; P_lenght=104 mm; Pilot_Dia_1=63 mm; Pilot_Dia_2=95 mm; Pilot_Dia_3=42 mm  [stored 0.137795 ft]; Pilot_Dia_4=21 mm  [stored 0.0688976 ft]; Pilot_Dia_5=14 mm  [stored 0.0459318 ft]; Pilot_top_1=628 mm; Pilot_top_ref=147 mm; Profile1_Height=355 mm; Profile1_Length=70 mm; Profile1_Length_2=47 mm; Profile_Dia=15 mm  [stored 0.0492126 ft]; Profile_Dia_2=15 mm  [stored 0.0492126 ft]; Profile_Dia_3=30 mm  [stored 0.0984252 ft]; Profile_height ref=50 mm; T_Height=380 mm; T_Height_2=326 mm; T_Height_Ref_1=54 mm; T_Height_Ref_2=63 mm; Top_Profile=452 mm; Top_Profile_Ref=457 mm; W=720 mm; W_Ref=503 mm; W_ref_2=675 mm
- 879-0400-10-04400051199_DN400_PN10: Body_Collar_Dia=115 mm; Body_Collar_Dia_2=99 mm; Body_Flange_Dia=314 mm; Body_Flange_Dia_2=344 mm; Body_Height_1=275 mm; Body_Height_2=138 mm; Body_Height_3=110 mm; Body_Height_4=153 mm; Body_Top_Dia=49 mm; Body_Top_Dia_2=41 mm  [stored 0.134514 ft]; Body_With_Dia=220 mm; Body_With_Dia_1=275 mm; Body_With_Dia_2=297 mm; Bolt_support=846 mm; Bolt_support_2=423 mm; Bolt_support_Dia=40 mm  [stored 0.131234 ft]; Bolt_support_lenght=220 mm; Bolt_support_lenght_2=230 mm; Bottom_profile=100 mm; D1=240 mm; D3=283 mm; D3_Ref=648 mm; DN=400 mm; Fillet_Length=20 mm  [stored 0.0656168 ft]; Flange_thickness=28 mm  [stored 0.0918635 ft]; H3=1010 mm; ID=200 mm; L=1100 mm; PG_Dia=133 mm; PG_Ref=183 mm; PG_depth=28 mm  [stored 0.0918635 ft]; PG_height=638 mm; PG_height_1=572 mm; PG_ref=220 mm; PR_1=65 mm; P_lenght=114 mm; Pilot_Dia_1=69 mm; Pilot_Dia_2=104 mm; Pilot_Dia_3=46 mm; Pilot_Dia_4=23 mm  [stored 0.0754593 ft]; Pilot_Dia_5=15 mm  [stored 0.0492126 ft]; Pilot_top_1=633 mm; Pilot_top_ref=85 mm; Profile1_Height=385 mm; Profile1_Length=76 mm; Profile1_Length_2=51 mm; Profile_Dia=20 mm  [stored 0.0656168 ft]; Profile_Dia_2=20 mm  [stored 0.0656168 ft]; Profile_Dia_3=40 mm  [stored 0.131234 ft]; Profile_height ref=55 mm; T_Height=288 mm; T_Height_2=246 mm; T_Height_Ref_1=41 mm  [stored 0.134514 ft]; T_Height_Ref_2=48 mm; Top_Profile=508 mm; Top_Profile_Ref=513 mm; W=790 mm; W_Ref=544 mm; W_ref_2=730 mm
- 879-0400-10-044000511A0_DN400_PN10: Body_Collar_Dia=115 mm; Body_Collar_Dia_2=99 mm; Body_Flange_Dia=314 mm; Body_Flange_Dia_2=344 mm; Body_Height_1=275 mm; Body_Height_2=138 mm; Body_Height_3=122 mm; Body_Height_4=153 mm; Body_Top_Dia=49 mm; Body_Top_Dia_2=41 mm  [stored 0.134514 ft]; Body_With_Dia=220 mm; Body_With_Dia_1=275 mm; Body_With_Dia_2=297 mm; Bolt_support=846 mm; Bolt_support_2=423 mm; Bolt_support_Dia=40 mm  [stored 0.131234 ft]; Bolt_support_lenght=220 mm; Bolt_support_lenght_2=230 mm; Bottom_profile=100 mm; D1=240 mm; D3=283 mm; D3_Ref=648 mm; DN=400 mm; Fillet_Length=20 mm  [stored 0.0656168 ft]; Flange_thickness=28 mm  [stored 0.0918635 ft]; H3=1183 mm; ID=200 mm; L=1100 mm; PG_Dia=133 mm; PG_Ref=183 mm; PG_depth=28 mm  [stored 0.0918635 ft]; PG_height=685 mm; PG_height_1=619 mm; PG_ref=220 mm; PR_1=102 mm; P_lenght=114 mm; Pilot_Dia_1=69 mm; Pilot_Dia_2=104 mm; Pilot_Dia_3=46 mm; Pilot_Dia_4=23 mm  [stored 0.0754593 ft]; Pilot_Dia_5=15 mm  [stored 0.0492126 ft]; Pilot_top_1=725 mm; Pilot_top_ref=166 mm; Profile1_Height=395 mm; Profile1_Length=76 mm; Profile1_Length_2=51 mm; Profile_Dia=20 mm  [stored 0.0656168 ft]; Profile_Dia_2=20 mm  [stored 0.0656168 ft]; Profile_Dia_3=40 mm  [stored 0.131234 ft]; Profile_height ref=55 mm; T_Height=451 mm; T_Height_2=386 mm; T_Height_Ref_1=64 mm; T_Height_Ref_2=75 mm; Top_Profile=508 mm; Top_Profile_Ref=513 mm; W=790 mm; W_Ref=544 mm; W_ref_2=730 mm
- 879-0400-10-14400051199_DN400_PN16: Body_Collar_Dia=115 mm; Body_Collar_Dia_2=99 mm; Body_Flange_Dia=314 mm; Body_Flange_Dia_2=344 mm; Body_Height_1=275 mm; Body_Height_2=138 mm; Body_Height_3=100 mm; Body_Height_4=153 mm; Body_Top_Dia=49 mm; Body_Top_Dia_2=41 mm  [stored 0.134514 ft]; Body_With_Dia=220 mm; Body_With_Dia_1=275 mm; Body_With_Dia_2=297 mm; Bolt_support=846 mm; Bolt_support_2=423 mm; Bolt_support_Dia=40 mm  [stored 0.131234 ft]; Bolt_support_lenght=220 mm; Bolt_support_lenght_2=230 mm; Bottom_profile=100 mm; D1=240 mm; D3=290 mm; D3_Ref=655 mm; DN=400 mm; Fillet_Length=20 mm  [stored 0.0656168 ft]; Flange_thickness=28 mm  [stored 0.0918635 ft]; H3=1010 mm; ID=200 mm; L=1100 mm; PG_Dia=133 mm; PG_Ref=183 mm; PG_depth=28 mm  [stored 0.0918635 ft]; PG_height=637 mm; PG_height_1=570 mm; PG_ref=220 mm; PR_1=63 mm; P_lenght=117 mm; Pilot_Dia_1=71 mm; Pilot_Dia_2=107 mm; Pilot_Dia_3=47 mm; Pilot_Dia_4=24 mm; Pilot_Dia_5=16 mm  [stored 0.0524934 ft]; Pilot_top_1=624 mm; Pilot_top_ref=86 mm; Profile1_Height=385 mm; Profile1_Length=78 mm; Profile1_Length_2=52 mm; Profile_Dia=20 mm  [stored 0.0656168 ft]; Profile_Dia_2=20 mm  [stored 0.0656168 ft]; Profile_Dia_3=40 mm  [stored 0.131234 ft]; Profile_height ref=55 mm; T_Height=280 mm; T_Height_2=240 mm; T_Height_Ref_1=40 mm  [stored 0.131234 ft]; T_Height_Ref_2=47 mm; Top_Profile=508 mm; Top_Profile_Ref=513 mm; W=790 mm; W_Ref=549 mm; W_ref_2=730 mm
- 879-0400-10-144000511A0_DN400_PN16: Body_Collar_Dia=115 mm; Body_Collar_Dia_2=99 mm; Body_Flange_Dia=314 mm; Body_Flange_Dia_2=344 mm; Body_Height_1=275 mm; Body_Height_2=138 mm; Body_Height_3=110 mm; Body_Height_4=153 mm; Body_Top_Dia=49 mm; Body_Top_Dia_2=41 mm  [stored 0.134514 ft]; Body_With_Dia=220 mm; Body_With_Dia_1=275 mm; Body_With_Dia_2=297 mm; Bolt_support=846 mm; Bolt_support_2=423 mm; Bolt_support_Dia=40 mm  [stored 0.131234 ft]; Bolt_support_lenght=220 mm; Bolt_support_lenght_2=230 mm; Bottom_profile=100 mm; D1=240 mm; D3=290 mm; D3_Ref=655 mm; DN=400 mm; Fillet_Length=20 mm  [stored 0.0656168 ft]; Flange_thickness=28 mm  [stored 0.0918635 ft]; H3=1183 mm; ID=200 mm; L=1100 mm; PG_Dia=133 mm; PG_Ref=183 mm; PG_depth=28 mm  [stored 0.0918635 ft]; PG_height=691 mm; PG_height_1=625 mm; PG_ref=220 mm; PR_1=98 mm; P_lenght=117 mm; Pilot_Dia_1=71 mm; Pilot_Dia_2=107 mm; Pilot_Dia_3=47 mm; Pilot_Dia_4=24 mm; Pilot_Dia_5=16 mm  [stored 0.0524934 ft]; Pilot_top_1=715 mm; Pilot_top_ref=168 mm; Profile1_Height=405 mm; Profile1_Length=78 mm; Profile1_Length_2=52 mm; Profile_Dia=20 mm  [stored 0.0656168 ft]; Profile_Dia_2=20 mm  [stored 0.0656168 ft]; Profile_Dia_3=40 mm  [stored 0.131234 ft]; Profile_height ref=55 mm; T_Height=433 mm; T_Height_2=371 mm; T_Height_Ref_1=62 mm; T_Height_Ref_2=72 mm; Top_Profile=508 mm; Top_Profile_Ref=513 mm; W=790 mm; W_Ref=549 mm; W_ref_2=730 mm
- 879-0450-10-04400051199_DN450_PN10: Body_Collar_Dia=125 mm; Body_Collar_Dia_2=108 mm; Body_Flange_Dia=343 mm; Body_Flange_Dia_2=375 mm; Body_Height_1=300 mm; Body_Height_2=150 mm; Body_Height_3=120 mm; Body_Height_4=165 mm; Body_Top_Dia=54 mm; Body_Top_Dia_2=45 mm; Body_With_Dia=240 mm; Body_With_Dia_1=300 mm; Body_With_Dia_2=324 mm; Bolt_support=923 mm; Bolt_support_2=462 mm; Bolt_support_Dia=40 mm  [stored 0.131234 ft]; Bolt_support_lenght=245 mm; Bolt_support_lenght_2=255 mm; Bottom_profile=113 mm; D1=265 mm; D3=308 mm; D3_Ref=748 mm; DN=450 mm; Fillet_Length=20 mm  [stored 0.0656168 ft]; Flange_thickness=30 mm  [stored 0.0984252 ft]; H3=1190 mm; ID=225 mm; L=1200 mm; PG_Dia=150 mm; PG_Ref=200 mm; PG_depth=28 mm  [stored 0.0918635 ft]; PG_height=737 mm; PG_height_1=662 mm; PG_ref=245 mm; PR_1=87 mm; P_lenght=125 mm; Pilot_Dia_1=76 mm; Pilot_Dia_2=113 mm; Pilot_Dia_3=50 mm; Pilot_Dia_4=25 mm  [stored 0.082021 ft]; Pilot_Dia_5=17 mm; Pilot_top_1=734 mm; Pilot_top_ref=139 mm; Profile1_Height=445 mm; Profile1_Length=83 mm; Profile1_Length_2=55 mm; Profile_Dia=20 mm  [stored 0.0656168 ft]; Profile_Dia_2=20 mm  [stored 0.0656168 ft]; Profile_Dia_3=40 mm  [stored 0.131234 ft]; Profile_height ref=55 mm; T_Height=383 mm; T_Height_2=328 mm; T_Height_Ref_1=55 mm; T_Height_Ref_2=64 mm; Top_Profile=554 mm; Top_Profile_Ref=559 mm; W=940 mm; W_Ref=634 mm; W_ref_2=880 mm
- 879-0450-10-044000511A0_DN450_PN10: Body_Collar_Dia=125 mm; Body_Collar_Dia_2=108 mm; Body_Flange_Dia=343 mm; Body_Flange_Dia_2=375 mm; Body_Height_1=300 mm; Body_Height_2=150 mm; Body_Height_3=120 mm; Body_Height_4=165 mm; Body_Top_Dia=54 mm; Body_Top_Dia_2=45 mm; Body_With_Dia=240 mm; Body_With_Dia_1=300 mm; Body_With_Dia_2=324 mm; Bolt_support=923 mm; Bolt_support_2=462 mm; Bolt_support_Dia=40 mm  [stored 0.131234 ft]; Bolt_support_lenght=245 mm; Bolt_support_lenght_2=255 mm; Bottom_profile=113 mm; D1=265 mm; D3=308 mm; D3_Ref=748 mm; DN=450 mm; Fillet_Length=20 mm  [stored 0.0656168 ft]; Flange_thickness=30 mm  [stored 0.0984252 ft]; H3=1361 mm; ID=225 mm; L=1200 mm; PG_Dia=150 mm; PG_Ref=200 mm; PG_depth=28 mm  [stored 0.0918635 ft]; PG_height=775 mm; PG_height_1=700 mm; PG_ref=245 mm; PR_1=125 mm; P_lenght=125 mm; Pilot_Dia_1=76 mm; Pilot_Dia_2=113 mm; Pilot_Dia_3=50 mm; Pilot_Dia_4=25 mm  [stored 0.082021 ft]; Pilot_Dia_5=17 mm; Pilot_top_1=819 mm; Pilot_top_ref=224 mm; Profile1_Height=445 mm; Profile1_Length=83 mm; Profile1_Length_2=55 mm; Profile_Dia=20 mm  [stored 0.0656168 ft]; Profile_Dia_2=20 mm  [stored 0.0656168 ft]; Profile_Dia_3=40 mm  [stored 0.131234 ft]; Profile_height ref=55 mm; T_Height=554 mm; T_Height_2=474 mm; T_Height_Ref_1=79 mm; T_Height_Ref_2=92 mm; Top_Profile=554 mm; Top_Profile_Ref=559 mm; W=940 mm; W_Ref=634 mm; W_ref_2=880 mm
- 879-0450-10-14400051199_DN450_PN16: Body_Collar_Dia=125 mm; Body_Collar_Dia_2=108 mm; Body_Flange_Dia=343 mm; Body_Flange_Dia_2=375 mm; Body_Height_1=300 mm; Body_Height_2=150 mm; Body_Height_3=120 mm; Body_Height_4=165 mm; Body_Top_Dia=54 mm; Body_Top_Dia_2=45 mm; Body_With_Dia=240 mm; Body_With_Dia_1=300 mm; Body_With_Dia_2=324 mm; Bolt_support=923 mm; Bolt_support_2=462 mm; Bolt_support_Dia=40 mm  [stored 0.131234 ft]; Bolt_support_lenght=245 mm; Bolt_support_lenght_2=255 mm; Bottom_profile=113 mm; D1=274 mm; D3=320 mm; D3_Ref=760 mm; DN=450 mm; Fillet_Length=20 mm  [stored 0.0656168 ft]; Flange_thickness=30 mm  [stored 0.0984252 ft]; H3=1190 mm; ID=225 mm; L=1200 mm; PG_Dia=150 mm; PG_Ref=200 mm; PG_depth=28 mm  [stored 0.0918635 ft]; PG_height=734 mm; PG_height_1=659 mm; PG_ref=245 mm; PR_1=84 mm; P_lenght=130 mm; Pilot_Dia_1=79 mm; Pilot_Dia_2=119 mm; Pilot_Dia_3=53 mm; Pilot_Dia_4=26 mm; Pilot_Dia_5=18 mm; Pilot_top_1=728 mm; Pilot_top_ref=133 mm; Profile1_Height=445 mm; Profile1_Length=86 mm; Profile1_Length_2=58 mm; Profile_Dia=20 mm  [stored 0.0656168 ft]; Profile_Dia_2=20 mm  [stored 0.0656168 ft]; Profile_Dia_3=40 mm  [stored 0.131234 ft]; Profile_height ref=55 mm; T_Height=370 mm; T_Height_2=317 mm; T_Height_Ref_1=53 mm; T_Height_Ref_2=62 mm; Top_Profile=554 mm; Top_Profile_Ref=559 mm; W=940 mm; W_Ref=642 mm; W_ref_2=880 mm
- 879-0450-10-144000511A0_DN450_PN16: Body_Collar_Dia=125 mm; Body_Collar_Dia_2=108 mm; Body_Flange_Dia=343 mm; Body_Flange_Dia_2=375 mm; Body_Height_1=300 mm; Body_Height_2=150 mm; Body_Height_3=120 mm; Body_Height_4=165 mm; Body_Top_Dia=54 mm; Body_Top_Dia_2=45 mm; Body_With_Dia=240 mm; Body_With_Dia_1=300 mm; Body_With_Dia_2=324 mm; Bolt_support=923 mm; Bolt_support_2=462 mm; Bolt_support_Dia=40 mm  [stored 0.131234 ft]; Bolt_support_lenght=245 mm; Bolt_support_lenght_2=255 mm; Bottom_profile=113 mm; D1=274 mm; D3=320 mm; D3_Ref=760 mm; DN=450 mm; Fillet_Length=20 mm  [stored 0.0656168 ft]; Flange_thickness=30 mm  [stored 0.0984252 ft]; H3=1361 mm; ID=225 mm; L=1200 mm; PG_Dia=150 mm; PG_Ref=200 mm; PG_depth=28 mm  [stored 0.0918635 ft]; PG_height=772 mm; PG_height_1=697 mm; PG_ref=245 mm; PR_1=122 mm; P_lenght=130 mm; Pilot_Dia_1=79 mm; Pilot_Dia_2=119 mm; Pilot_Dia_3=53 mm; Pilot_Dia_4=26 mm; Pilot_Dia_5=18 mm; Pilot_top_1=813 mm; Pilot_top_ref=218 mm; Profile1_Height=445 mm; Profile1_Length=86 mm; Profile1_Length_2=58 mm; Profile_Dia=20 mm  [stored 0.0656168 ft]; Profile_Dia_2=20 mm  [stored 0.0656168 ft]; Profile_Dia_3=40 mm  [stored 0.131234 ft]; Profile_height ref=55 mm; T_Height=541 mm; T_Height_2=464 mm; T_Height_Ref_1=77 mm; T_Height_Ref_2=90 mm; Top_Profile=554 mm; Top_Profile_Ref=559 mm; W=940 mm; W_Ref=642 mm; W_ref_2=880 mm
- 879-0500-10-04400051199_DN500_PN10: Body_Collar_Dia=130 mm; Body_Collar_Dia_2=112 mm; Body_Flange_Dia=357 mm; Body_Flange_Dia_2=391 mm; Body_Height_1=313 mm; Body_Height_2=156 mm; Body_Height_3=125 mm; Body_Height_4=171 mm; Body_Top_Dia=56 mm; Body_Top_Dia_2=47 mm; Body_With_Dia=250 mm; Body_With_Dia_1=313 mm; Body_With_Dia_2=338 mm; Bolt_support=962 mm; Bolt_support_2=481 mm; Bolt_support_Dia=50 mm; Bolt_support_lenght=270 mm; Bolt_support_lenght_2=280 mm; Bottom_profile=125 mm; D1=291 mm; D3=335 mm; D3_Ref=813 mm; DN=500 mm; Fillet_Length=25 mm  [stored 0.082021 ft]; Flange_thickness=32 mm; H3=1265 mm; ID=250 mm; L=1250 mm; PG_Dia=167 mm; PG_Ref=208 mm; PG_depth=35 mm  [stored 0.114829 ft]; PG_height=772 mm; PG_height_1=688 mm; PG_ref=270 mm; PR_1=95 mm; P_lenght=137 mm; Pilot_Dia_1=83 mm; Pilot_Dia_2=125 mm; Pilot_Dia_3=55 mm; Pilot_Dia_4=28 mm  [stored 0.0918635 ft]; Pilot_Dia_5=18 mm; Pilot_top_1=769 mm; Pilot_top_ref=151 mm; Profile1_Height=450 mm; Profile1_Length=91 mm; Profile1_Length_2=60 mm; Profile_Dia=25 mm  [stored 0.082021 ft]; Profile_Dia_2=25 mm  [stored 0.082021 ft]; Profile_Dia_3=50 mm; Profile_height ref=60 mm; T_Height=420 mm; T_Height_2=360 mm; T_Height_Ref_1=60 mm; T_Height_Ref_2=70 mm; Top_Profile=577 mm; Top_Profile_Ref=582 mm; W=1030 mm; W_Ref=688 mm; W_ref_2=955 mm
- 879-0500-10-044000511A0_DN500_PN10: Body_Collar_Dia=130 mm; Body_Collar_Dia_2=112 mm; Body_Flange_Dia=357 mm; Body_Flange_Dia_2=391 mm; Body_Height_1=313 mm; Body_Height_2=156 mm; Body_Height_3=125 mm; Body_Height_4=171 mm; Body_Top_Dia=56 mm; Body_Top_Dia_2=47 mm; Body_With_Dia=250 mm; Body_With_Dia_1=313 mm; Body_With_Dia_2=338 mm; Bolt_support=962 mm; Bolt_support_2=481 mm; Bolt_support_Dia=50 mm; Bolt_support_lenght=270 mm; Bolt_support_lenght_2=280 mm; Bottom_profile=125 mm; D1=291 mm; D3=335 mm; D3_Ref=813 mm; DN=500 mm; Fillet_Length=25 mm  [stored 0.082021 ft]; Flange_thickness=32 mm; H3=1435 mm; ID=250 mm; L=1250 mm; PG_Dia=167 mm; PG_Ref=208 mm; PG_depth=35 mm  [stored 0.114829 ft]; PG_height=822 mm; PG_height_1=738 mm; PG_ref=270 mm; PR_1=130 mm; P_lenght=137 mm; Pilot_Dia_1=83 mm; Pilot_Dia_2=125 mm; Pilot_Dia_3=55 mm; Pilot_Dia_4=28 mm  [stored 0.0918635 ft]; Pilot_Dia_5=18 mm; Pilot_top_1=854 mm; Pilot_top_ref=236 mm; Profile1_Height=465 mm; Profile1_Length=91 mm; Profile1_Length_2=60 mm; Profile_Dia=25 mm  [stored 0.082021 ft]; Profile_Dia_2=25 mm  [stored 0.082021 ft]; Profile_Dia_3=50 mm; Profile_height ref=60 mm; T_Height=575 mm; T_Height_2=493 mm; T_Height_Ref_1=82 mm; T_Height_Ref_2=96 mm; Top_Profile=577 mm; Top_Profile_Ref=582 mm; W=1030 mm; W_Ref=688 mm; W_ref_2=955 mm
- 879-0500-10-14400051199_DN500_PN16: Body_Collar_Dia=130 mm; Body_Collar_Dia_2=112 mm; Body_Flange_Dia=357 mm; Body_Flange_Dia_2=391 mm; Body_Height_1=313 mm; Body_Height_2=156 mm; Body_Height_3=125 mm; Body_Height_4=171 mm; Body_Top_Dia=56 mm; Body_Top_Dia_2=47 mm; Body_With_Dia=250 mm; Body_With_Dia_1=313 mm; Body_With_Dia_2=338 mm; Bolt_support=962 mm; Bolt_support_2=481 mm; Bolt_support_Dia=50 mm; Bolt_support_lenght=270 mm; Bolt_support_lenght_2=280 mm; Bottom_profile=125 mm; D1=305 mm; D3=358 mm; D3_Ref=835 mm; DN=500 mm; Fillet_Length=25 mm  [stored 0.082021 ft]; Flange_thickness=32 mm; H3=1265 mm; ID=250 mm; L=1250 mm; PG_Dia=167 mm; PG_Ref=208 mm; PG_depth=35 mm  [stored 0.114829 ft]; PG_height=771 mm; PG_height_1=687 mm; PG_ref=270 mm; PR_1=89 mm; P_lenght=147 mm; Pilot_Dia_1=89 mm; Pilot_Dia_2=134 mm; Pilot_Dia_3=59 mm; Pilot_Dia_4=30 mm  [stored 0.0984252 ft]; Pilot_Dia_5=20 mm  [stored 0.0656168 ft]; Pilot_top_1=758 mm; Pilot_top_ref=139 mm; Profile1_Height=455 mm; Profile1_Length=97 mm; Profile1_Length_2=64 mm; Profile_Dia=25 mm  [stored 0.082021 ft]; Profile_Dia_2=25 mm  [stored 0.082021 ft]; Profile_Dia_3=50 mm; Profile_height ref=60 mm; T_Height=393 mm; T_Height_2=336 mm; T_Height_Ref_1=56 mm; T_Height_Ref_2=65 mm; Top_Profile=577 mm; Top_Profile_Ref=582 mm; W=1030 mm; W_Ref=702 mm; W_ref_2=955 mm
- 879-0500-10-144000511A0_DN500_PN16: Body_Collar_Dia=130 mm; Body_Collar_Dia_2=112 mm; Body_Flange_Dia=357 mm; Body_Flange_Dia_2=391 mm; Body_Height_1=313 mm; Body_Height_2=156 mm; Body_Height_3=125 mm; Body_Height_4=171 mm; Body_Top_Dia=56 mm; Body_Top_Dia_2=47 mm; Body_With_Dia=250 mm; Body_With_Dia_1=313 mm; Body_With_Dia_2=338 mm; Bolt_support=962 mm; Bolt_support_2=481 mm; Bolt_support_Dia=50 mm; Bolt_support_lenght=270 mm; Bolt_support_lenght_2=280 mm; Bottom_profile=125 mm; D1=305 mm; D3=358 mm; D3_Ref=835 mm; DN=500 mm; Fillet_Length=25 mm  [stored 0.082021 ft]; Flange_thickness=32 mm; H3=1435 mm; ID=250 mm; L=1250 mm; PG_Dia=167 mm; PG_Ref=208 mm; PG_depth=35 mm  [stored 0.114829 ft]; PG_height=809 mm; PG_height_1=726 mm; PG_ref=270 mm; PR_1=127 mm; P_lenght=147 mm; Pilot_Dia_1=89 mm; Pilot_Dia_2=134 mm; Pilot_Dia_3=59 mm; Pilot_Dia_4=30 mm  [stored 0.0984252 ft]; Pilot_Dia_5=20 mm  [stored 0.0656168 ft]; Pilot_top_1=843 mm; Pilot_top_ref=224 mm; Profile1_Height=455 mm; Profile1_Length=97 mm; Profile1_Length_2=64 mm; Profile_Dia=25 mm  [stored 0.082021 ft]; Profile_Dia_2=25 mm  [stored 0.082021 ft]; Profile_Dia_3=50 mm; Profile_height ref=60 mm; T_Height=563 mm; T_Height_2=482 mm; T_Height_Ref_1=80 mm; T_Height_Ref_2=94 mm; Top_Profile=577 mm; Top_Profile_Ref=582 mm; W=1030 mm; W_Ref=702 mm; W_ref_2=955 mm
- 879-0600-10-04400051199_DN600_PN10: Body_Collar_Dia=151 mm; Body_Collar_Dia_2=130 mm; Body_Flange_Dia=414 mm; Body_Flange_Dia_2=453 mm; Body_Height_1=363 mm; Body_Height_2=181 mm; Body_Height_3=145 mm; Body_Height_4=196 mm; Body_Top_Dia=65 mm; Body_Top_Dia_2=54 mm; Body_With_Dia=290 mm; Body_With_Dia_1=363 mm; Body_With_Dia_2=392 mm; Bolt_support=1115 mm; Bolt_support_2=558 mm; Bolt_support_Dia=60 mm; Bolt_support_lenght=320 mm; Bolt_support_lenght_2=330 mm; Bottom_profile=150 mm; D1=341 mm; D3=390 mm; D3_Ref=945 mm; DN=600 mm; Fillet_Length=30 mm  [stored 0.0984252 ft]; Flange_thickness=36 mm  [stored 0.11811 ft]; H3=1410 mm; ID=300 mm; L=1450 mm; PG_Dia=200 mm; PG_Ref=242 mm; PG_depth=42 mm  [stored 0.137795 ft]; PG_height=887 mm; PG_height_1=787 mm; PG_ref=320 mm; PR_1=97 mm; P_lenght=162 mm; Pilot_Dia_1=98 mm; Pilot_Dia_2=147 mm; Pilot_Dia_3=65 mm; Pilot_Dia_4=33 mm  [stored 0.108268 ft]; Pilot_Dia_5=22 mm  [stored 0.0721785 ft]; Pilot_top_1=862 mm; Pilot_top_ref=148 mm; Profile1_Height=525 mm; Profile1_Length=105 mm; Profile1_Length_2=70 mm; Profile_Dia=30 mm  [stored 0.0984252 ft]; Profile_Dia_2=30 mm  [stored 0.0984252 ft]; Profile_Dia_3=60 mm; Profile_height ref=65 mm; T_Height=430 mm; T_Height_2=369 mm; T_Height_Ref_1=61 mm; T_Height_Ref_2=72 mm; Top_Profile=669 mm; Top_Profile_Ref=674 mm; W=1200 mm; W_Ref=798 mm; W_ref_2=1110 mm
- 879-0600-10-044000511A0_DN600_PN10: Body_Collar_Dia=151 mm; Body_Collar_Dia_2=130 mm; Body_Flange_Dia=414 mm; Body_Flange_Dia_2=453 mm; Body_Height_1=363 mm; Body_Height_2=181 mm; Body_Height_3=145 mm; Body_Height_4=196 mm; Body_Top_Dia=65 mm; Body_Top_Dia_2=54 mm; Body_With_Dia=290 mm; Body_With_Dia_1=363 mm; Body_With_Dia_2=392 mm; Bolt_support=1115 mm; Bolt_support_2=558 mm; Bolt_support_Dia=60 mm; Bolt_support_lenght=320 mm; Bolt_support_lenght_2=330 mm; Bottom_profile=150 mm; D1=341 mm; D3=390 mm; D3_Ref=945 mm; DN=600 mm; Fillet_Length=30 mm  [stored 0.0984252 ft]; Flange_thickness=36 mm  [stored 0.11811 ft]; H3=1584 mm; ID=300 mm; L=1450 mm; PG_Dia=200 mm; PG_Ref=242 mm; PG_depth=42 mm  [stored 0.137795 ft]; PG_height=934 mm; PG_height_1=834 mm; PG_ref=320 mm; PR_1=134 mm; P_lenght=162 mm; Pilot_Dia_1=98 mm; Pilot_Dia_2=147 mm; Pilot_Dia_3=65 mm; Pilot_Dia_4=33 mm  [stored 0.108268 ft]; Pilot_Dia_5=22 mm  [stored 0.0721785 ft]; Pilot_top_1=949 mm; Pilot_top_ref=235 mm; Profile1_Height=535 mm; Profile1_Length=105 mm; Profile1_Length_2=70 mm; Profile_Dia=30 mm  [stored 0.0984252 ft]; Profile_Dia_2=30 mm  [stored 0.0984252 ft]; Profile_Dia_3=60 mm; Profile_height ref=65 mm; T_Height=594 mm; T_Height_2=509 mm; T_Height_Ref_1=85 mm; T_Height_Ref_2=99 mm; Top_Profile=669 mm; Top_Profile_Ref=674 mm; W=1200 mm; W_Ref=798 mm; W_ref_2=1110 mm
- 879-0600-10-14400051199_DN600_PN16: Body_Collar_Dia=151 mm; Body_Collar_Dia_2=130 mm; Body_Flange_Dia=414 mm; Body_Flange_Dia_2=453 mm; Body_Height_1=363 mm; Body_Height_2=181 mm; Body_Height_3=145 mm; Body_Height_4=196 mm; Body_Top_Dia=65 mm; Body_Top_Dia_2=54 mm; Body_With_Dia=290 mm; Body_With_Dia_1=363 mm; Body_With_Dia_2=392 mm; Bolt_support=1115 mm; Bolt_support_2=558 mm; Bolt_support_Dia=60 mm; Bolt_support_lenght=320 mm; Bolt_support_lenght_2=330 mm; Bottom_profile=150 mm; D1=360 mm; D3=420 mm; D3_Ref=975 mm; DN=600 mm; Fillet_Length=30 mm  [stored 0.0984252 ft]; Flange_thickness=36 mm  [stored 0.11811 ft]; H3=1410 mm; ID=300 mm; L=1450 mm; PG_Dia=200 mm; PG_Ref=242 mm; PG_depth=42 mm  [stored 0.137795 ft]; PG_height=884 mm; PG_height_1=784 mm; PG_ref=320 mm; PR_1=89 mm; P_lenght=175 mm; Pilot_Dia_1=106 mm; Pilot_Dia_2=159 mm; Pilot_Dia_3=71 mm; Pilot_Dia_4=35 mm  [stored 0.114829 ft]; Pilot_Dia_5=24 mm; Pilot_top_1=847 mm; Pilot_top_ref=133 mm; Profile1_Height=530 mm; Profile1_Length=114 mm; Profile1_Length_2=76 mm; Profile_Dia=30 mm  [stored 0.0984252 ft]; Profile_Dia_2=30 mm  [stored 0.0984252 ft]; Profile_Dia_3=60 mm; Profile_height ref=65 mm; T_Height=395 mm; T_Height_2=339 mm; T_Height_Ref_1=56 mm; T_Height_Ref_2=66 mm; Top_Profile=669 mm; Top_Profile_Ref=674 mm; W=1200 mm; W_Ref=816 mm; W_ref_2=1110 mm
- 879-0600-10-144000511A0_DN600_PN16: Body_Collar_Dia=151 mm; Body_Collar_Dia_2=130 mm; Body_Flange_Dia=414 mm; Body_Flange_Dia_2=453 mm; Body_Height_1=363 mm; Body_Height_2=181 mm; Body_Height_3=145 mm; Body_Height_4=196 mm; Body_Top_Dia=65 mm; Body_Top_Dia_2=54 mm; Body_With_Dia=290 mm; Body_With_Dia_1=363 mm; Body_With_Dia_2=392 mm; Bolt_support=1115 mm; Bolt_support_2=558 mm; Bolt_support_Dia=60 mm; Bolt_support_lenght=320 mm; Bolt_support_lenght_2=330 mm; Bottom_profile=150 mm; D1=360 mm; D3=420 mm; D3_Ref=975 mm; DN=600 mm; Fillet_Length=30 mm  [stored 0.0984252 ft]; Flange_thickness=36 mm  [stored 0.11811 ft]; H3=1584 mm; ID=300 mm; L=1450 mm; PG_Dia=200 mm; PG_Ref=242 mm; PG_depth=42 mm  [stored 0.137795 ft]; PG_height=928 mm; PG_height_1=828 mm; PG_ref=320 mm; PR_1=128 mm; P_lenght=175 mm; Pilot_Dia_1=106 mm; Pilot_Dia_2=159 mm; Pilot_Dia_3=71 mm; Pilot_Dia_4=35 mm  [stored 0.114829 ft]; Pilot_Dia_5=24 mm; Pilot_top_1=934 mm; Pilot_top_ref=220 mm; Profile1_Height=535 mm; Profile1_Length=114 mm; Profile1_Length_2=76 mm; Profile_Dia=30 mm  [stored 0.0984252 ft]; Profile_Dia_2=30 mm  [stored 0.0984252 ft]; Profile_Dia_3=60 mm; Profile_height ref=65 mm; T_Height=564 mm; T_Height_2=483 mm; T_Height_Ref_1=81 mm; T_Height_Ref_2=94 mm; Top_Profile=669 mm; Top_Profile_Ref=674 mm; W=1200 mm; W_Ref=816 mm; W_ref_2=1110 mm

note: [stored X ft] marks values corroborated as IEEE doubles in the binary element streams (Revit-internal decimal feet)

## geometry (parser evidence)
native form markers: Sweep x4
no freeform markers — native parametric forms only
